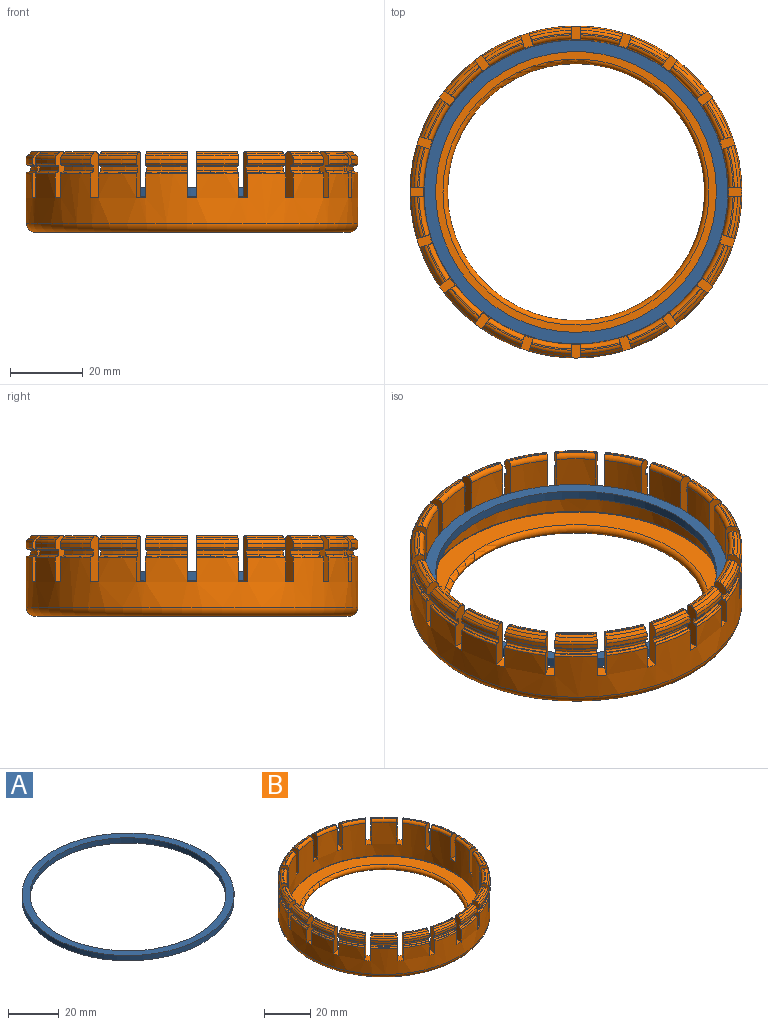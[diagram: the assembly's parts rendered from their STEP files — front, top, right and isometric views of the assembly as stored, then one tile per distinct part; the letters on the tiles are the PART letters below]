
ASSEMBLY  parts=2 mates=1
PART A: 4 faces, bbox 83.7x83.7x2.5 mm
  f0: cylinder r=38.67mm len=77.34mm, axis (0,0,-1), area 617.2mm2, adj f2,f3
  f1: cylinder r=41.85mm len=83.69mm, axis (0,0,-1), area 667.8mm2, adj f2,f3
  f2: plane 83.69x83.69mm, normal (0,0,1), area 803.1mm2, adj f0,f1
  f3: plane 83.69x83.69mm, normal (0,0,-1), area 803.1mm2, adj f0,f1
PART B: 329 faces, bbox 99x99x22.2 mm
  f0: plane 11.49x2.06mm, normal (0,0,1), area 3mm2, adj f126,f184,f262,f263
  f1: cylinder r=44.45mm len=11.25mm, axis (0,0,1), area 10.2mm2, adj f126,f184,f263,f264
  f2: plane 11.49x2.06mm, normal (0,0,-1), area 3mm2, adj f126,f184,f264,f265
  f3: cylinder r=45.72mm len=11.65mm, axis (0,0,1), area 13.5mm2, adj f126,f184,f265,f325
  f4: cone r=45.72mm half-angle=45deg, axis (0,0,-1), area 13mm2, adj f126,f184,f325,f326
  f5: plane 10.05x5.36mm, normal (0,0,1), area 4.2mm2, adj f181,f183,f268,f269
  f6: plane 10.44x5.49mm, normal (0,0,1), area 3mm2, adj f181,f183,f186,f189
  f7: cylinder r=44.45mm len=10.15mm, axis (0,0,1), area 10.2mm2, adj f181,f183,f186,f187
  f8: plane 10.44x5.49mm, normal (0,0,-1), area 3mm2, adj f181,f183,f187,f188
  f9: cylinder r=45.72mm len=10.51mm, axis (0,0,1), area 13.5mm2, adj f181,f183,f188,f267
  f10: cone r=45.72mm half-angle=45deg, axis (0,0,-1), area 13mm2, adj f181,f183,f267,f268
  f11: plane 8.1x8.1mm, normal (0,0,1), area 4.2mm2, adj f178,f180,f271,f272
  f12: plane 8.37x8.37mm, normal (0,0,1), area 3mm2, adj f178,f180,f190,f193
  f13: cylinder r=44.45mm len=8.06mm, axis (0,0,1), area 10.2mm2, adj f178,f180,f190,f191
  f14: plane 8.37x8.37mm, normal (0,0,-1), area 3mm2, adj f178,f180,f191,f192
  f15: cylinder r=45.72mm len=8.34mm, axis (0,0,1), area 13.5mm2, adj f178,f180,f192,f270
  f16: cone r=45.72mm half-angle=45deg, axis (0,0,-1), area 13mm2, adj f178,f180,f270,f271
  f17: plane 10.05x5.36mm, normal (0,0,1), area 4.2mm2, adj f175,f177,f274,f275
  f18: plane 10.44x5.49mm, normal (0,0,1), area 3mm2, adj f175,f177,f194,f197
  f19: cylinder r=44.45mm len=10.15mm, axis (0,0,1), area 10.2mm2, adj f175,f177,f194,f195
  f20: plane 10.44x5.49mm, normal (0,0,-1), area 3mm2, adj f175,f177,f195,f196
  f21: cylinder r=45.72mm len=10.51mm, axis (0,0,1), area 13.5mm2, adj f175,f177,f196,f273
  f22: cone r=45.72mm half-angle=45deg, axis (0,0,-1), area 13mm2, adj f175,f177,f273,f274
  f23: plane 11.01x2.1mm, normal (0,0,1), area 4.2mm2, adj f172,f174,f277,f278
  f24: plane 11.49x2.06mm, normal (0,0,1), area 3mm2, adj f172,f174,f198,f201
  f25: cylinder r=44.45mm len=11.25mm, axis (0,0,1), area 10.2mm2, adj f172,f174,f198,f199
  f26: plane 11.49x2.06mm, normal (0,0,-1), area 3mm2, adj f172,f174,f199,f200
  f27: cylinder r=45.72mm len=11.65mm, axis (0,0,1), area 13.5mm2, adj f172,f174,f200,f276
  f28: cone r=45.72mm half-angle=45deg, axis (0,0,-1), area 13mm2, adj f172,f174,f276,f277
  f29: plane 11.01x2.1mm, normal (0,0,1), area 4.2mm2, adj f169,f171,f280,f281
  f30: plane 11.49x2.06mm, normal (0,0,1), area 3mm2, adj f169,f171,f202,f205
  f31: cylinder r=44.45mm len=11.25mm, axis (0,0,1), area 10.2mm2, adj f169,f171,f202,f203
  f32: plane 11.49x2.06mm, normal (0,0,-1), area 3mm2, adj f169,f171,f203,f204
  f33: cylinder r=45.72mm len=11.65mm, axis (0,0,1), area 13.5mm2, adj f169,f171,f204,f279
  f34: cone r=45.72mm half-angle=45deg, axis (0,0,-1), area 13mm2, adj f169,f171,f279,f280
  f35: plane 10.05x5.36mm, normal (0,0,1), area 4.2mm2, adj f166,f168,f283,f284
  f36: plane 10.44x5.49mm, normal (0,0,1), area 3mm2, adj f166,f168,f206,f209
  f37: cylinder r=44.45mm len=10.15mm, axis (0,0,1), area 10.2mm2, adj f166,f168,f206,f207
  f38: plane 10.44x5.49mm, normal (0,0,-1), area 3mm2, adj f166,f168,f207,f208
  f39: cylinder r=45.72mm len=10.51mm, axis (0,0,1), area 13.5mm2, adj f166,f168,f208,f282
  f40: cone r=45.72mm half-angle=45deg, axis (0,0,-1), area 13mm2, adj f166,f168,f282,f283
  f41: plane 8.1x8.1mm, normal (0,0,1), area 4.2mm2, adj f163,f165,f286,f287
  f42: plane 8.37x8.37mm, normal (0,0,1), area 3mm2, adj f163,f165,f210,f213
  f43: cylinder r=44.45mm len=8.06mm, axis (0,0,1), area 10.2mm2, adj f163,f165,f210,f211
  f44: plane 8.37x8.37mm, normal (0,0,-1), area 3mm2, adj f163,f165,f211,f212
  f45: cylinder r=45.72mm len=8.34mm, axis (0,0,1), area 13.5mm2, adj f163,f165,f212,f285
  f46: cone r=45.72mm half-angle=45deg, axis (0,0,-1), area 13mm2, adj f163,f165,f285,f286
  f47: plane 10.05x5.36mm, normal (0,0,1), area 4.2mm2, adj f160,f162,f289,f290
  f48: plane 10.44x5.49mm, normal (0,0,1), area 3mm2, adj f160,f162,f214,f217
  f49: cylinder r=44.45mm len=10.15mm, axis (0,0,1), area 10.2mm2, adj f160,f162,f214,f215
  f50: plane 10.44x5.49mm, normal (0,0,-1), area 3mm2, adj f160,f162,f215,f216
  f51: cylinder r=45.72mm len=10.51mm, axis (0,0,1), area 13.5mm2, adj f160,f162,f216,f288
  f52: cone r=45.72mm half-angle=45deg, axis (0,0,-1), area 13mm2, adj f160,f162,f288,f289
  f53: plane 11.01x2.1mm, normal (0,0,1), area 4.2mm2, adj f157,f159,f292,f293
  f54: plane 11.49x2.06mm, normal (0,0,1), area 3mm2, adj f157,f159,f218,f221
  f55: cylinder r=44.45mm len=11.25mm, axis (0,0,1), area 10.2mm2, adj f157,f159,f218,f219
  f56: plane 11.49x2.06mm, normal (0,0,-1), area 3mm2, adj f157,f159,f219,f220
  f57: cylinder r=45.72mm len=11.65mm, axis (0,0,1), area 13.5mm2, adj f157,f159,f220,f291
  f58: cone r=45.72mm half-angle=45deg, axis (0,0,-1), area 13mm2, adj f157,f159,f291,f292
  f59: plane 11.01x2.1mm, normal (0,0,1), area 4.2mm2, adj f154,f156,f295,f296
  f60: plane 11.49x2.06mm, normal (0,0,1), area 3mm2, adj f154,f156,f222,f225
  f61: cylinder r=44.45mm len=11.25mm, axis (0,0,1), area 10.2mm2, adj f154,f156,f222,f223
  f62: plane 11.49x2.06mm, normal (0,0,-1), area 3mm2, adj f154,f156,f223,f224
  f63: cylinder r=45.72mm len=11.65mm, axis (0,0,1), area 13.5mm2, adj f154,f156,f224,f294
  f64: cone r=45.72mm half-angle=45deg, axis (0,0,-1), area 13mm2, adj f154,f156,f294,f295
  f65: plane 10.05x5.36mm, normal (0,0,1), area 4.2mm2, adj f151,f153,f298,f299
  f66: plane 10.44x5.49mm, normal (0,0,1), area 3mm2, adj f151,f153,f226,f229
  f67: cylinder r=44.45mm len=10.15mm, axis (0,0,1), area 10.2mm2, adj f151,f153,f226,f227
  f68: plane 10.44x5.49mm, normal (0,0,-1), area 3mm2, adj f151,f153,f227,f228
  f69: cylinder r=45.72mm len=10.51mm, axis (0,0,1), area 13.5mm2, adj f151,f153,f228,f297
  f70: cone r=45.72mm half-angle=45deg, axis (0,0,-1), area 13mm2, adj f151,f153,f297,f298
  f71: plane 8.1x8.1mm, normal (0,0,1), area 4.2mm2, adj f148,f150,f301,f302
  f72: plane 8.37x8.37mm, normal (0,0,1), area 3mm2, adj f148,f150,f230,f233
  f73: cylinder r=44.45mm len=8.06mm, axis (0,0,1), area 10.2mm2, adj f148,f150,f230,f231
  f74: plane 8.37x8.37mm, normal (0,0,-1), area 3mm2, adj f148,f150,f231,f232
  f75: cylinder r=45.72mm len=8.34mm, axis (0,0,1), area 13.5mm2, adj f148,f150,f232,f300
  f76: cone r=45.72mm half-angle=45deg, axis (0,0,-1), area 13mm2, adj f148,f150,f300,f301
  f77: plane 10.05x5.36mm, normal (0,0,1), area 4.2mm2, adj f145,f147,f304,f305
  f78: plane 10.44x5.49mm, normal (0,0,1), area 3mm2, adj f145,f147,f234,f237
  f79: cylinder r=44.45mm len=10.15mm, axis (0,0,1), area 10.2mm2, adj f145,f147,f234,f235
  f80: plane 10.44x5.49mm, normal (0,0,-1), area 3mm2, adj f145,f147,f235,f236
  f81: cylinder r=45.72mm len=10.51mm, axis (0,0,1), area 13.5mm2, adj f145,f147,f236,f303
  f82: cone r=45.72mm half-angle=45deg, axis (0,0,-1), area 13mm2, adj f145,f147,f303,f304
  f83: plane 11.01x2.1mm, normal (0,0,1), area 4.2mm2, adj f142,f144,f307,f308
  f84: plane 11.49x2.06mm, normal (0,0,1), area 3mm2, adj f142,f144,f238,f241
  f85: cylinder r=44.45mm len=11.25mm, axis (0,0,1), area 10.2mm2, adj f142,f144,f238,f239
  f86: plane 11.49x2.06mm, normal (0,0,-1), area 3mm2, adj f142,f144,f239,f240
  f87: cylinder r=45.72mm len=11.65mm, axis (0,0,1), area 13.5mm2, adj f142,f144,f240,f306
  f88: cone r=45.72mm half-angle=45deg, axis (0,0,-1), area 13mm2, adj f142,f144,f306,f307
  f89: plane 11.01x2.1mm, normal (0,0,1), area 4.2mm2, adj f139,f141,f310,f311
  f90: plane 11.49x2.06mm, normal (0,0,1), area 3mm2, adj f139,f141,f242,f245
  f91: cylinder r=44.45mm len=11.25mm, axis (0,0,1), area 10.2mm2, adj f139,f141,f242,f243
  f92: plane 11.49x2.06mm, normal (0,0,-1), area 3mm2, adj f139,f141,f243,f244
  f93: cylinder r=45.72mm len=11.65mm, axis (0,0,1), area 13.5mm2, adj f139,f141,f244,f309
  f94: cone r=45.72mm half-angle=45deg, axis (0,0,-1), area 13mm2, adj f139,f141,f309,f310
  f95: plane 10.05x5.36mm, normal (0,0,1), area 4.2mm2, adj f136,f138,f313,f314
  f96: plane 10.44x5.49mm, normal (0,0,1), area 3mm2, adj f136,f138,f246,f249
  f97: cylinder r=44.45mm len=10.15mm, axis (0,0,1), area 10.2mm2, adj f136,f138,f246,f247
  f98: plane 10.44x5.49mm, normal (0,0,-1), area 3mm2, adj f136,f138,f247,f248
  f99: cylinder r=45.72mm len=10.51mm, axis (0,0,1), area 13.5mm2, adj f136,f138,f248,f312
  f100: cone r=45.72mm half-angle=45deg, axis (0,0,-1), area 13mm2, adj f136,f138,f312,f313
  f101: plane 8.1x8.1mm, normal (0,0,1), area 4.2mm2, adj f133,f135,f316,f317
  f102: plane 8.37x8.37mm, normal (0,0,1), area 3mm2, adj f133,f135,f250,f253
  f103: cylinder r=44.45mm len=8.06mm, axis (0,0,1), area 10.2mm2, adj f133,f135,f250,f251
  f104: plane 8.37x8.37mm, normal (0,0,-1), area 3mm2, adj f133,f135,f251,f252
  f105: cylinder r=45.72mm len=8.34mm, axis (0,0,1), area 13.5mm2, adj f133,f135,f252,f315
  f106: cone r=45.72mm half-angle=45deg, axis (0,0,-1), area 13mm2, adj f133,f135,f315,f316
  f107: plane 10.05x5.36mm, normal (0,0,1), area 4.2mm2, adj f130,f132,f319,f320
  f108: plane 11.01x2.1mm, normal (0,0,1), area 4.2mm2, adj f127,f129,f322,f323
  f109: plane 10.44x5.49mm, normal (0,0,1), area 3mm2, adj f130,f132,f254,f257
  f110: cylinder r=44.45mm len=10.15mm, axis (0,0,1), area 10.2mm2, adj f130,f132,f254,f255
  f111: plane 10.44x5.49mm, normal (0,0,-1), area 3mm2, adj f130,f132,f255,f256
  f112: cylinder r=45.72mm len=10.51mm, axis (0,0,1), area 13.5mm2, adj f130,f132,f256,f318
  f113: cone r=45.72mm half-angle=45deg, axis (0,0,-1), area 13mm2, adj f130,f132,f318,f319
  f114: plane 11.01x2.1mm, normal (0,0,1), area 4.2mm2, adj f126,f184,f326,f327
  f115: plane 86.36x86.36mm, normal (0,0,-1), area 1640.1mm2, adj f324,f328
  f116: cylinder r=45.72mm len=91.44mm, axis (0,0,1), area 3562.1mm2, adj f126,f127,f128,f129,f130,f131,f132,f133
  f117: plane 11.49x2.06mm, normal (0,0,1), area 3mm2, adj f127,f129,f258,f259
  f118: cylinder r=44.45mm len=11.25mm, axis (0,0,1), area 10.2mm2, adj f127,f129,f259,f260
  f119: plane 11.49x2.06mm, normal (0,0,-1), area 3mm2, adj f127,f129,f260,f261
  f120: cylinder r=45.72mm len=11.65mm, axis (0,0,1), area 13.5mm2, adj f127,f129,f261,f321
  f121: cone r=45.72mm half-angle=45deg, axis (0,0,-1), area 13mm2, adj f127,f129,f321,f322
  f122: cylinder r=42.01mm len=84.02mm, axis (0,0,1), area 4079.1mm2, adj f126,f127,f128,f129,f130,f131,f132,f133
  f123: plane 87.73x87.73mm, normal (0,0,-1), area 365.3mm2, adj f124,f266
  f124: cylinder r=43.87mm len=87.73mm, axis (0,0,1), area 70mm2, adj f123,f125
  f125: plane 87.73x87.73mm, normal (0,0,1), area 1827.6mm2, adj f124,f324
  f126: plane 12.72x3.73mm, normal (1,0,0), area 43.1mm2, adj f0,f1,f2,f3,f4,f114,f116,f122
  f127: plane 12.72x3.73mm, normal (-1,0,0), area 43.1mm2, adj f108,f116,f117,f118,f119,f120,f121,f122
  f128: plane 3.73x2.54mm, normal (0,0,1), area 9.4mm2, adj f116,f122,f126,f127
  f129: plane 12.72x3.54mm, normal (0.95,-0.31,0), area 43.1mm2, adj f108,f116,f117,f118,f119,f120,f121,f122
  f130: plane 12.72x3.54mm, normal (-0.95,0.31,0), area 43.1mm2, adj f107,f109,f110,f111,f112,f113,f116,f122
  f131: plane 4.31x3.56mm, normal (0,0,1), area 9.4mm2, adj f116,f122,f129,f130
  f132: plane 12.72x3.02mm, normal (0.81,-0.59,0), area 43.1mm2, adj f107,f109,f110,f111,f112,f113,f116,f122
  f133: plane 12.72x3.02mm, normal (-0.81,0.59,0), area 43.1mm2, adj f101,f102,f103,f104,f105,f106,f116,f122
  f134: plane 4.49x4.24mm, normal (0,0,1), area 9.4mm2, adj f116,f122,f132,f133
  f135: plane 12.72x3.02mm, normal (0.59,-0.81,0), area 43.1mm2, adj f101,f102,f103,f104,f105,f106,f116,f122
  f136: plane 12.72x3.02mm, normal (-0.59,0.81,0), area 43.1mm2, adj f95,f96,f97,f98,f99,f100,f116,f122
  f137: plane 4.49x4.24mm, normal (0,0,1), area 9.4mm2, adj f116,f122,f135,f136
  f138: plane 12.72x3.54mm, normal (0.31,-0.95,0), area 43.1mm2, adj f95,f96,f97,f98,f99,f100,f116,f122
  f139: plane 12.72x3.54mm, normal (-0.31,0.95,0), area 43.1mm2, adj f89,f90,f91,f92,f93,f94,f116,f122
  f140: plane 4.31x3.56mm, normal (0,0,1), area 9.4mm2, adj f116,f122,f138,f139
  f141: plane 12.72x3.73mm, normal (0,-1,0), area 43.1mm2, adj f89,f90,f91,f92,f93,f94,f116,f122
  f142: plane 12.72x3.73mm, normal (0,1,0), area 43.1mm2, adj f83,f84,f85,f86,f87,f88,f116,f122
  f143: plane 3.73x2.54mm, normal (0,0,1), area 9.4mm2, adj f116,f122,f141,f142
  f144: plane 12.72x3.54mm, normal (-0.31,-0.95,0), area 43.1mm2, adj f83,f84,f85,f86,f87,f88,f116,f122
  f145: plane 12.72x3.54mm, normal (0.31,0.95,0), area 43.1mm2, adj f77,f78,f79,f80,f81,f82,f116,f122
  f146: plane 4.31x3.56mm, normal (0,0,1), area 9.4mm2, adj f116,f122,f144,f145
  f147: plane 12.72x3.02mm, normal (-0.59,-0.81,0), area 43.1mm2, adj f77,f78,f79,f80,f81,f82,f116,f122
  f148: plane 12.72x3.02mm, normal (0.59,0.81,0), area 43.1mm2, adj f71,f72,f73,f74,f75,f76,f116,f122
  f149: plane 4.49x4.24mm, normal (0,0,1), area 9.4mm2, adj f116,f122,f147,f148
  f150: plane 12.72x3.02mm, normal (-0.81,-0.59,0), area 43.1mm2, adj f71,f72,f73,f74,f75,f76,f116,f122
  f151: plane 12.72x3.02mm, normal (0.81,0.59,0), area 43.1mm2, adj f65,f66,f67,f68,f69,f70,f116,f122
  f152: plane 4.49x4.24mm, normal (0,0,1), area 9.4mm2, adj f116,f122,f150,f151
  f153: plane 12.72x3.54mm, normal (-0.95,-0.31,0), area 43.1mm2, adj f65,f66,f67,f68,f69,f70,f116,f122
  f154: plane 12.72x3.54mm, normal (0.95,0.31,0), area 43.1mm2, adj f59,f60,f61,f62,f63,f64,f116,f122
  f155: plane 4.31x3.56mm, normal (0,0,1), area 9.4mm2, adj f116,f122,f153,f154
  f156: plane 12.72x3.73mm, normal (-1,0,0), area 43.1mm2, adj f59,f60,f61,f62,f63,f64,f116,f122
  f157: plane 12.72x3.73mm, normal (1,0,0), area 43.1mm2, adj f53,f54,f55,f56,f57,f58,f116,f122
  f158: plane 3.73x2.54mm, normal (0,0,1), area 9.4mm2, adj f116,f122,f156,f157
  f159: plane 12.72x3.54mm, normal (-0.95,0.31,0), area 43.1mm2, adj f53,f54,f55,f56,f57,f58,f116,f122
  f160: plane 12.72x3.54mm, normal (0.95,-0.31,0), area 43.1mm2, adj f47,f48,f49,f50,f51,f52,f116,f122
  f161: plane 4.31x3.56mm, normal (0,0,1), area 9.4mm2, adj f116,f122,f159,f160
  f162: plane 12.72x3.02mm, normal (-0.81,0.59,0), area 43.1mm2, adj f47,f48,f49,f50,f51,f52,f116,f122
  f163: plane 12.72x3.02mm, normal (0.81,-0.59,0), area 43.1mm2, adj f41,f42,f43,f44,f45,f46,f116,f122
  f164: plane 4.49x4.24mm, normal (0,0,1), area 9.4mm2, adj f116,f122,f162,f163
  f165: plane 12.72x3.02mm, normal (-0.59,0.81,0), area 43.1mm2, adj f41,f42,f43,f44,f45,f46,f116,f122
  f166: plane 12.72x3.02mm, normal (0.59,-0.81,0), area 43.1mm2, adj f35,f36,f37,f38,f39,f40,f116,f122
  f167: plane 4.49x4.24mm, normal (0,0,1), area 9.4mm2, adj f116,f122,f165,f166
  f168: plane 12.72x3.54mm, normal (-0.31,0.95,0), area 43.1mm2, adj f35,f36,f37,f38,f39,f40,f116,f122
  f169: plane 12.72x3.54mm, normal (0.31,-0.95,0), area 43.1mm2, adj f29,f30,f31,f32,f33,f34,f116,f122
  f170: plane 4.31x3.56mm, normal (0,0,1), area 9.4mm2, adj f116,f122,f168,f169
  f171: plane 12.72x3.73mm, normal (0,1,0), area 43.1mm2, adj f29,f30,f31,f32,f33,f34,f116,f122
  f172: plane 12.72x3.73mm, normal (0,-1,0), area 43.1mm2, adj f23,f24,f25,f26,f27,f28,f116,f122
  f173: plane 3.73x2.54mm, normal (0,0,1), area 9.4mm2, adj f116,f122,f171,f172
  f174: plane 12.72x3.54mm, normal (0.31,0.95,0), area 43.1mm2, adj f23,f24,f25,f26,f27,f28,f116,f122
  f175: plane 12.72x3.54mm, normal (-0.31,-0.95,0), area 43.1mm2, adj f17,f18,f19,f20,f21,f22,f116,f122
  f176: plane 4.31x3.56mm, normal (0,0,1), area 9.4mm2, adj f116,f122,f174,f175
  f177: plane 12.72x3.02mm, normal (0.59,0.81,0), area 43.1mm2, adj f17,f18,f19,f20,f21,f22,f116,f122
  f178: plane 12.72x3.02mm, normal (-0.59,-0.81,0), area 43.1mm2, adj f11,f12,f13,f14,f15,f16,f116,f122
  f179: plane 4.49x4.24mm, normal (0,0,1), area 9.4mm2, adj f116,f122,f177,f178
  f180: plane 12.72x3.02mm, normal (0.81,0.59,0), area 43.1mm2, adj f11,f12,f13,f14,f15,f16,f116,f122
  f181: plane 12.72x3.02mm, normal (-0.81,-0.59,0), area 43.1mm2, adj f5,f6,f7,f8,f9,f10,f116,f122
  f182: plane 4.49x4.24mm, normal (0,0,1), area 9.4mm2, adj f116,f122,f180,f181
  f183: plane 12.72x3.54mm, normal (0.95,0.31,0), area 43.1mm2, adj f5,f6,f7,f8,f9,f10,f116,f122
  f184: plane 12.72x3.54mm, normal (-0.95,-0.31,0), area 43.1mm2, adj f0,f1,f2,f3,f4,f114,f116,f122
  f185: plane 4.31x3.56mm, normal (0,0,1), area 9.4mm2, adj f116,f122,f183,f184
  f186: torus R=44.96mm, axis (0,0,-1), area 9.2mm2, adj f6,f7,f181,f183
  f187: torus R=44.96mm, axis (0,0,1), area 9.2mm2, adj f7,f8,f181,f183
  f188: torus R=45.21mm, axis (0,0,1), area 9.4mm2, adj f8,f9,f181,f183
  f189: torus R=45.21mm, axis (0,0,-1), area 9.4mm2, adj f6,f116,f181,f183
  f190: torus R=44.96mm, axis (0,0,-1), area 9.2mm2, adj f12,f13,f178,f180
  f191: torus R=44.96mm, axis (0,0,1), area 9.2mm2, adj f13,f14,f178,f180
  f192: torus R=45.21mm, axis (0,0,1), area 9.4mm2, adj f14,f15,f178,f180
  f193: torus R=45.21mm, axis (0,0,-1), area 9.4mm2, adj f12,f116,f178,f180
  f194: torus R=44.96mm, axis (0,0,-1), area 9.2mm2, adj f18,f19,f175,f177
  f195: torus R=44.96mm, axis (0,0,1), area 9.2mm2, adj f19,f20,f175,f177
  f196: torus R=45.21mm, axis (0,0,1), area 9.4mm2, adj f20,f21,f175,f177
  f197: torus R=45.21mm, axis (0,0,-1), area 9.4mm2, adj f18,f116,f175,f177
  f198: torus R=44.96mm, axis (0,0,-1), area 9.2mm2, adj f24,f25,f172,f174
  f199: torus R=44.96mm, axis (0,0,1), area 9.2mm2, adj f25,f26,f172,f174
  f200: torus R=45.21mm, axis (0,0,1), area 9.4mm2, adj f26,f27,f172,f174
  f201: torus R=45.21mm, axis (0,0,-1), area 9.4mm2, adj f24,f116,f172,f174
  f202: torus R=44.96mm, axis (0,0,-1), area 9.2mm2, adj f30,f31,f169,f171
  f203: torus R=44.96mm, axis (0,0,1), area 9.2mm2, adj f31,f32,f169,f171
  f204: torus R=45.21mm, axis (0,0,1), area 9.4mm2, adj f32,f33,f169,f171
  f205: torus R=45.21mm, axis (0,0,-1), area 9.4mm2, adj f30,f116,f169,f171
  f206: torus R=44.96mm, axis (0,0,-1), area 9.2mm2, adj f36,f37,f166,f168
  f207: torus R=44.96mm, axis (0,0,1), area 9.2mm2, adj f37,f38,f166,f168
  f208: torus R=45.21mm, axis (0,0,1), area 9.4mm2, adj f38,f39,f166,f168
  f209: torus R=45.21mm, axis (0,0,-1), area 9.4mm2, adj f36,f116,f166,f168
  f210: torus R=44.96mm, axis (0,0,-1), area 9.2mm2, adj f42,f43,f163,f165
  f211: torus R=44.96mm, axis (0,0,1), area 9.2mm2, adj f43,f44,f163,f165
  f212: torus R=45.21mm, axis (0,0,1), area 9.4mm2, adj f44,f45,f163,f165
  f213: torus R=45.21mm, axis (0,0,-1), area 9.4mm2, adj f42,f116,f163,f165
  f214: torus R=44.96mm, axis (0,0,-1), area 9.2mm2, adj f48,f49,f160,f162
  f215: torus R=44.96mm, axis (0,0,1), area 9.2mm2, adj f49,f50,f160,f162
  f216: torus R=45.21mm, axis (0,0,1), area 9.4mm2, adj f50,f51,f160,f162
  f217: torus R=45.21mm, axis (0,0,-1), area 9.4mm2, adj f48,f116,f160,f162
  f218: torus R=44.96mm, axis (0,0,-1), area 9.2mm2, adj f54,f55,f157,f159
  f219: torus R=44.96mm, axis (0,0,1), area 9.2mm2, adj f55,f56,f157,f159
  f220: torus R=45.21mm, axis (0,0,1), area 9.4mm2, adj f56,f57,f157,f159
  f221: torus R=45.21mm, axis (0,0,-1), area 9.4mm2, adj f54,f116,f157,f159
  f222: torus R=44.96mm, axis (0,0,-1), area 9.2mm2, adj f60,f61,f154,f156
  f223: torus R=44.96mm, axis (0,0,1), area 9.2mm2, adj f61,f62,f154,f156
  f224: torus R=45.21mm, axis (0,0,1), area 9.4mm2, adj f62,f63,f154,f156
  f225: torus R=45.21mm, axis (0,0,-1), area 9.4mm2, adj f60,f116,f154,f156
  f226: torus R=44.96mm, axis (0,0,-1), area 9.2mm2, adj f66,f67,f151,f153
  f227: torus R=44.96mm, axis (0,0,1), area 9.2mm2, adj f67,f68,f151,f153
  f228: torus R=45.21mm, axis (0,0,1), area 9.4mm2, adj f68,f69,f151,f153
  f229: torus R=45.21mm, axis (0,0,-1), area 9.4mm2, adj f66,f116,f151,f153
  f230: torus R=44.96mm, axis (0,0,-1), area 9.2mm2, adj f72,f73,f148,f150
  f231: torus R=44.96mm, axis (0,0,1), area 9.2mm2, adj f73,f74,f148,f150
  f232: torus R=45.21mm, axis (0,0,1), area 9.4mm2, adj f74,f75,f148,f150
  f233: torus R=45.21mm, axis (0,0,-1), area 9.4mm2, adj f72,f116,f148,f150
  f234: torus R=44.96mm, axis (0,0,-1), area 9.2mm2, adj f78,f79,f145,f147
  f235: torus R=44.96mm, axis (0,0,1), area 9.2mm2, adj f79,f80,f145,f147
  f236: torus R=45.21mm, axis (0,0,1), area 9.4mm2, adj f80,f81,f145,f147
  f237: torus R=45.21mm, axis (0,0,-1), area 9.4mm2, adj f78,f116,f145,f147
  f238: torus R=44.96mm, axis (0,0,-1), area 9.2mm2, adj f84,f85,f142,f144
  f239: torus R=44.96mm, axis (0,0,1), area 9.2mm2, adj f85,f86,f142,f144
  f240: torus R=45.21mm, axis (0,0,1), area 9.4mm2, adj f86,f87,f142,f144
  f241: torus R=45.21mm, axis (0,0,-1), area 9.4mm2, adj f84,f116,f142,f144
  f242: torus R=44.96mm, axis (0,0,-1), area 9.2mm2, adj f90,f91,f139,f141
  f243: torus R=44.96mm, axis (0,0,1), area 9.2mm2, adj f91,f92,f139,f141
  f244: torus R=45.21mm, axis (0,0,1), area 9.4mm2, adj f92,f93,f139,f141
  f245: torus R=45.21mm, axis (0,0,-1), area 9.4mm2, adj f90,f116,f139,f141
  f246: torus R=44.96mm, axis (0,0,-1), area 9.2mm2, adj f96,f97,f136,f138
  f247: torus R=44.96mm, axis (0,0,1), area 9.2mm2, adj f97,f98,f136,f138
  f248: torus R=45.21mm, axis (0,0,1), area 9.4mm2, adj f98,f99,f136,f138
  f249: torus R=45.21mm, axis (0,0,-1), area 9.4mm2, adj f96,f116,f136,f138
  f250: torus R=44.96mm, axis (0,0,-1), area 9.2mm2, adj f102,f103,f133,f135
  f251: torus R=44.96mm, axis (0,0,1), area 9.2mm2, adj f103,f104,f133,f135
  f252: torus R=45.21mm, axis (0,0,1), area 9.4mm2, adj f104,f105,f133,f135
  f253: torus R=45.21mm, axis (0,0,-1), area 9.4mm2, adj f102,f116,f133,f135
  f254: torus R=44.96mm, axis (0,0,-1), area 9.2mm2, adj f109,f110,f130,f132
  f255: torus R=44.96mm, axis (0,0,1), area 9.2mm2, adj f110,f111,f130,f132
  f256: torus R=45.21mm, axis (0,0,1), area 9.4mm2, adj f111,f112,f130,f132
  f257: torus R=45.21mm, axis (0,0,-1), area 9.4mm2, adj f109,f116,f130,f132
  f258: torus R=45.21mm, axis (0,0,-1), area 9.4mm2, adj f116,f117,f127,f129
  f259: torus R=44.96mm, axis (0,0,-1), area 9.2mm2, adj f117,f118,f127,f129
  f260: torus R=44.96mm, axis (0,0,1), area 9.2mm2, adj f118,f119,f127,f129
  f261: torus R=45.21mm, axis (0,0,1), area 9.4mm2, adj f119,f120,f127,f129
  f262: torus R=45.21mm, axis (0,0,-1), area 9.4mm2, adj f0,f116,f126,f184
  f263: torus R=44.96mm, axis (0,0,-1), area 9.2mm2, adj f0,f1,f126,f184
  f264: torus R=44.96mm, axis (0,0,1), area 9.2mm2, adj f1,f2,f126,f184
  f265: torus R=45.21mm, axis (0,0,1), area 9.4mm2, adj f2,f3,f126,f184
  f266: torus R=42.52mm, axis (0,0,1), area 211.6mm2, adj f122,f123
  f267: torus R=44.45mm, axis (0,0,-1), area 11.7mm2, adj f9,f10,f181,f183
  f268: torus R=43.66mm, axis (0,0,-1), area 11.3mm2, adj f5,f10,f181,f183
  f269: torus R=43.28mm, axis (0,0,-1), area 21.6mm2, adj f5,f122,f181,f183
  f270: torus R=44.45mm, axis (0,0,-1), area 11.7mm2, adj f15,f16,f178,f180
  f271: torus R=43.66mm, axis (0,0,-1), area 11.3mm2, adj f11,f16,f178,f180
  f272: torus R=43.28mm, axis (0,0,-1), area 21.6mm2, adj f11,f122,f178,f180
  f273: torus R=44.45mm, axis (0,0,-1), area 11.7mm2, adj f21,f22,f175,f177
  f274: torus R=43.66mm, axis (0,0,-1), area 11.3mm2, adj f17,f22,f175,f177
  f275: torus R=43.28mm, axis (0,0,-1), area 21.6mm2, adj f17,f122,f175,f177
  f276: torus R=44.45mm, axis (0,0,-1), area 11.7mm2, adj f27,f28,f172,f174
  f277: torus R=43.66mm, axis (0,0,-1), area 11.3mm2, adj f23,f28,f172,f174
  f278: torus R=43.28mm, axis (0,0,-1), area 21.6mm2, adj f23,f122,f172,f174
  f279: torus R=44.45mm, axis (0,0,-1), area 11.7mm2, adj f33,f34,f169,f171
  f280: torus R=43.66mm, axis (0,0,-1), area 11.3mm2, adj f29,f34,f169,f171
  f281: torus R=43.28mm, axis (0,0,-1), area 21.6mm2, adj f29,f122,f169,f171
  f282: torus R=44.45mm, axis (0,0,-1), area 11.7mm2, adj f39,f40,f166,f168
  f283: torus R=43.66mm, axis (0,0,-1), area 11.3mm2, adj f35,f40,f166,f168
  f284: torus R=43.28mm, axis (0,0,-1), area 21.6mm2, adj f35,f122,f166,f168
  f285: torus R=44.45mm, axis (0,0,-1), area 11.7mm2, adj f45,f46,f163,f165
  f286: torus R=43.66mm, axis (0,0,-1), area 11.3mm2, adj f41,f46,f163,f165
  f287: torus R=43.28mm, axis (0,0,-1), area 21.6mm2, adj f41,f122,f163,f165
  f288: torus R=44.45mm, axis (0,0,-1), area 11.7mm2, adj f51,f52,f160,f162
  f289: torus R=43.66mm, axis (0,0,-1), area 11.3mm2, adj f47,f52,f160,f162
  f290: torus R=43.28mm, axis (0,0,-1), area 21.6mm2, adj f47,f122,f160,f162
  f291: torus R=44.45mm, axis (0,0,-1), area 11.7mm2, adj f57,f58,f157,f159
  f292: torus R=43.66mm, axis (0,0,-1), area 11.3mm2, adj f53,f58,f157,f159
  f293: torus R=43.28mm, axis (0,0,-1), area 21.6mm2, adj f53,f122,f157,f159
  f294: torus R=44.45mm, axis (0,0,-1), area 11.7mm2, adj f63,f64,f154,f156
  f295: torus R=43.66mm, axis (0,0,-1), area 11.3mm2, adj f59,f64,f154,f156
  f296: torus R=43.28mm, axis (0,0,-1), area 21.6mm2, adj f59,f122,f154,f156
  f297: torus R=44.45mm, axis (0,0,-1), area 11.7mm2, adj f69,f70,f151,f153
  f298: torus R=43.66mm, axis (0,0,-1), area 11.3mm2, adj f65,f70,f151,f153
  f299: torus R=43.28mm, axis (0,0,-1), area 21.6mm2, adj f65,f122,f151,f153
  f300: torus R=44.45mm, axis (0,0,-1), area 11.7mm2, adj f75,f76,f148,f150
  f301: torus R=43.66mm, axis (0,0,-1), area 11.3mm2, adj f71,f76,f148,f150
  f302: torus R=43.28mm, axis (0,0,-1), area 21.6mm2, adj f71,f122,f148,f150
  f303: torus R=44.45mm, axis (0,0,-1), area 11.7mm2, adj f81,f82,f145,f147
  f304: torus R=43.66mm, axis (0,0,-1), area 11.3mm2, adj f77,f82,f145,f147
  f305: torus R=43.28mm, axis (0,0,-1), area 21.6mm2, adj f77,f122,f145,f147
  f306: torus R=44.45mm, axis (0,0,-1), area 11.7mm2, adj f87,f88,f142,f144
  f307: torus R=43.66mm, axis (0,0,-1), area 11.3mm2, adj f83,f88,f142,f144
  f308: torus R=43.28mm, axis (0,0,-1), area 21.6mm2, adj f83,f122,f142,f144
  f309: torus R=44.45mm, axis (0,0,-1), area 11.7mm2, adj f93,f94,f139,f141
  f310: torus R=43.66mm, axis (0,0,-1), area 11.3mm2, adj f89,f94,f139,f141
  f311: torus R=43.28mm, axis (0,0,-1), area 21.6mm2, adj f89,f122,f139,f141
  f312: torus R=44.45mm, axis (0,0,-1), area 11.7mm2, adj f99,f100,f136,f138
  f313: torus R=43.66mm, axis (0,0,-1), area 11.3mm2, adj f95,f100,f136,f138
  f314: torus R=43.28mm, axis (0,0,-1), area 21.6mm2, adj f95,f122,f136,f138
  f315: torus R=44.45mm, axis (0,0,-1), area 11.7mm2, adj f105,f106,f133,f135
  f316: torus R=43.66mm, axis (0,0,-1), area 11.3mm2, adj f101,f106,f133,f135
  f317: torus R=43.28mm, axis (0,0,-1), area 21.6mm2, adj f101,f122,f133,f135
  f318: torus R=44.45mm, axis (0,0,-1), area 11.7mm2, adj f112,f113,f130,f132
  f319: torus R=43.66mm, axis (0,0,-1), area 11.3mm2, adj f107,f113,f130,f132
  f320: torus R=43.28mm, axis (0,0,-1), area 21.6mm2, adj f107,f122,f130,f132
  f321: torus R=44.45mm, axis (0,0,-1), area 11.7mm2, adj f120,f121,f127,f129
  f322: torus R=43.66mm, axis (0,0,-1), area 11.3mm2, adj f108,f121,f127,f129
  f323: torus R=43.28mm, axis (0,0,-1), area 21.6mm2, adj f108,f122,f127,f129
  f324: torus R=36.64mm, axis (0,0,-1), area 898.2mm2, adj f115,f125
  f325: torus R=44.45mm, axis (0,0,-1), area 11.7mm2, adj f3,f4,f126,f184
  f326: torus R=43.66mm, axis (0,0,-1), area 11.3mm2, adj f4,f114,f126,f184
  f327: torus R=43.28mm, axis (0,0,-1), area 21.6mm2, adj f114,f122,f126,f184
  f328: torus R=43.18mm, axis (0,0,1), area 1123mm2, adj f115,f116
PLACE A rot(axis=(0,0,1),15.4deg) t=(0,0,1.82)mm
PLACE B t=(0,0,-9.32)mm
MATE cylindrical A.f1 <-> B.f1  axis (0,0,-1) through (0,0,1.82)mm
